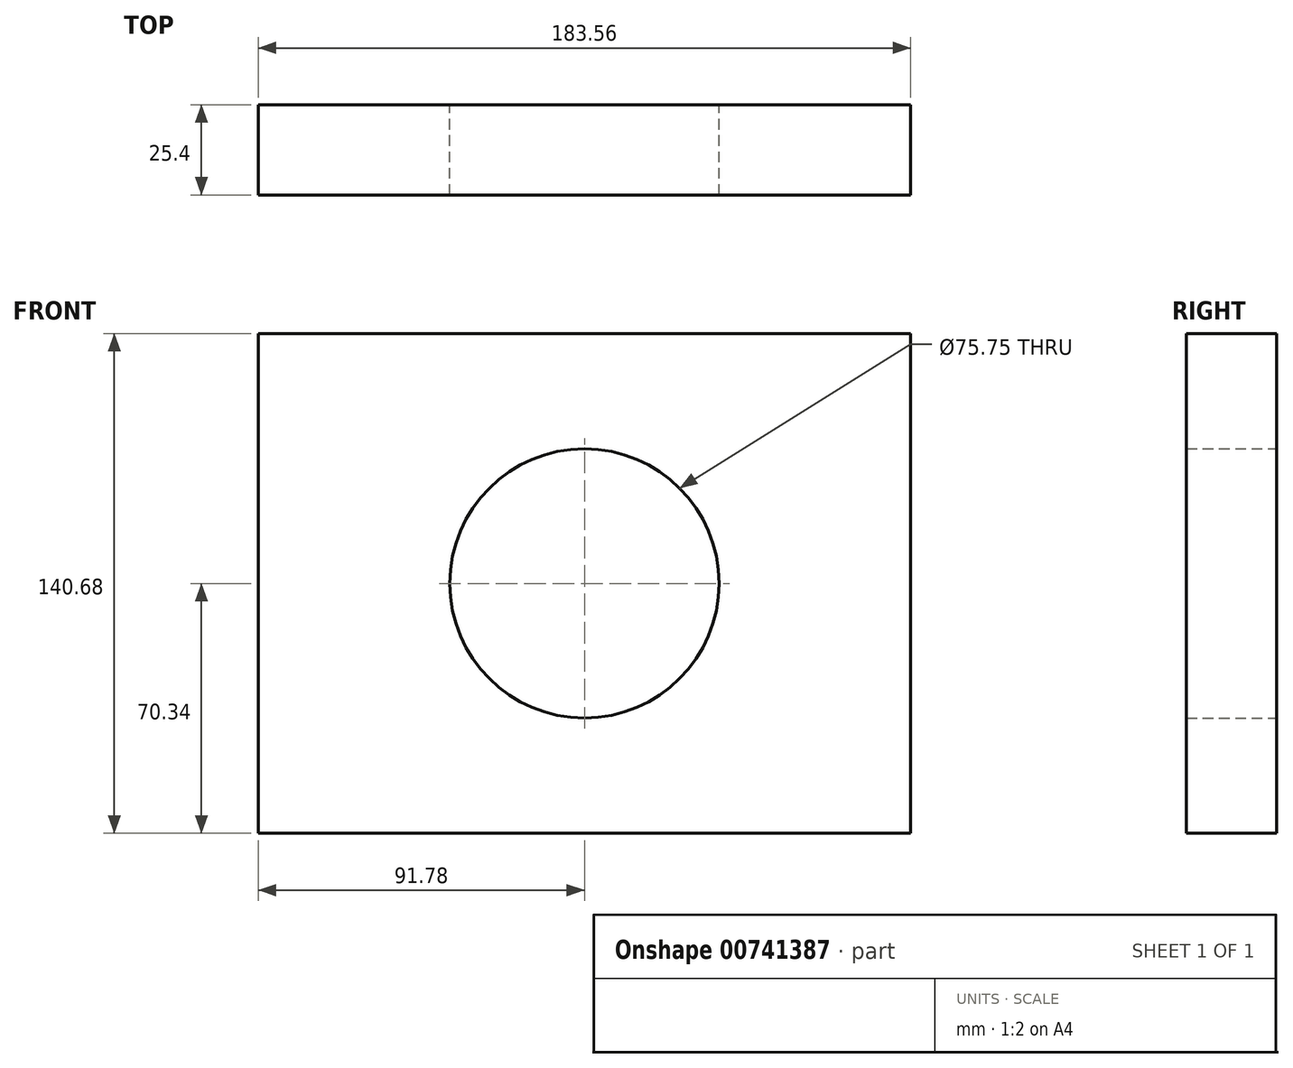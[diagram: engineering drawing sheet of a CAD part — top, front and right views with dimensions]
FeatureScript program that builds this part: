
annotation { "Feature Type Name" : "Feature", "Feature Type Description" : "" }
export const myFeature = defineFeature(function(context is Context, id is Id, definition is map)
    precondition{}
    {
        {
            var Q0;
            Q0=qCreatedBy(makeId("Front.planeOp"),FACE);
            var sketch = newSketch(context, id + "F0", { "sketchPlane" : qUnion([Q0])});
            skLineSegment(sketch, "E0.bottom", {"start": v(91.78, 70.34) * mm, "end": v(-91.78, 70.34) * mm});
            skLineSegment(sketch, "E0.top", {"start": v(91.78, -70.34) * mm, "end": v(-91.78, -70.34) * mm});
            skLineSegment(sketch, "E0.left", {"start": v(91.78, 70.34) * mm, "end": v(91.78, -70.34) * mm});
            skLineSegment(sketch, "E0.right", {"start": v(-91.78, 70.34) * mm, "end": v(-91.78, -70.34) * mm});
            skPoint(sketch, "E0.middle", {"position": v(0, 0) * mm});
            skCircle(sketch, "E1", {"center": v(0, 0) * mm, "radius": 37.88 * mm});
            skLineSegment(sketch, "E2", {"start": v(0, 0) * mm, "end": v(75.92, 0) * mm});
            skSolve(sketch);
        }
        {
            var Q0;
            Q0 = qSketchRegion(id + "F0", true);
            extrude(context, id + "F1", {"entities" : qUnion([Q0]), "depth" : 25.4 * mm, "offsetDistance" : 25.4 * mm});
        }
    });
